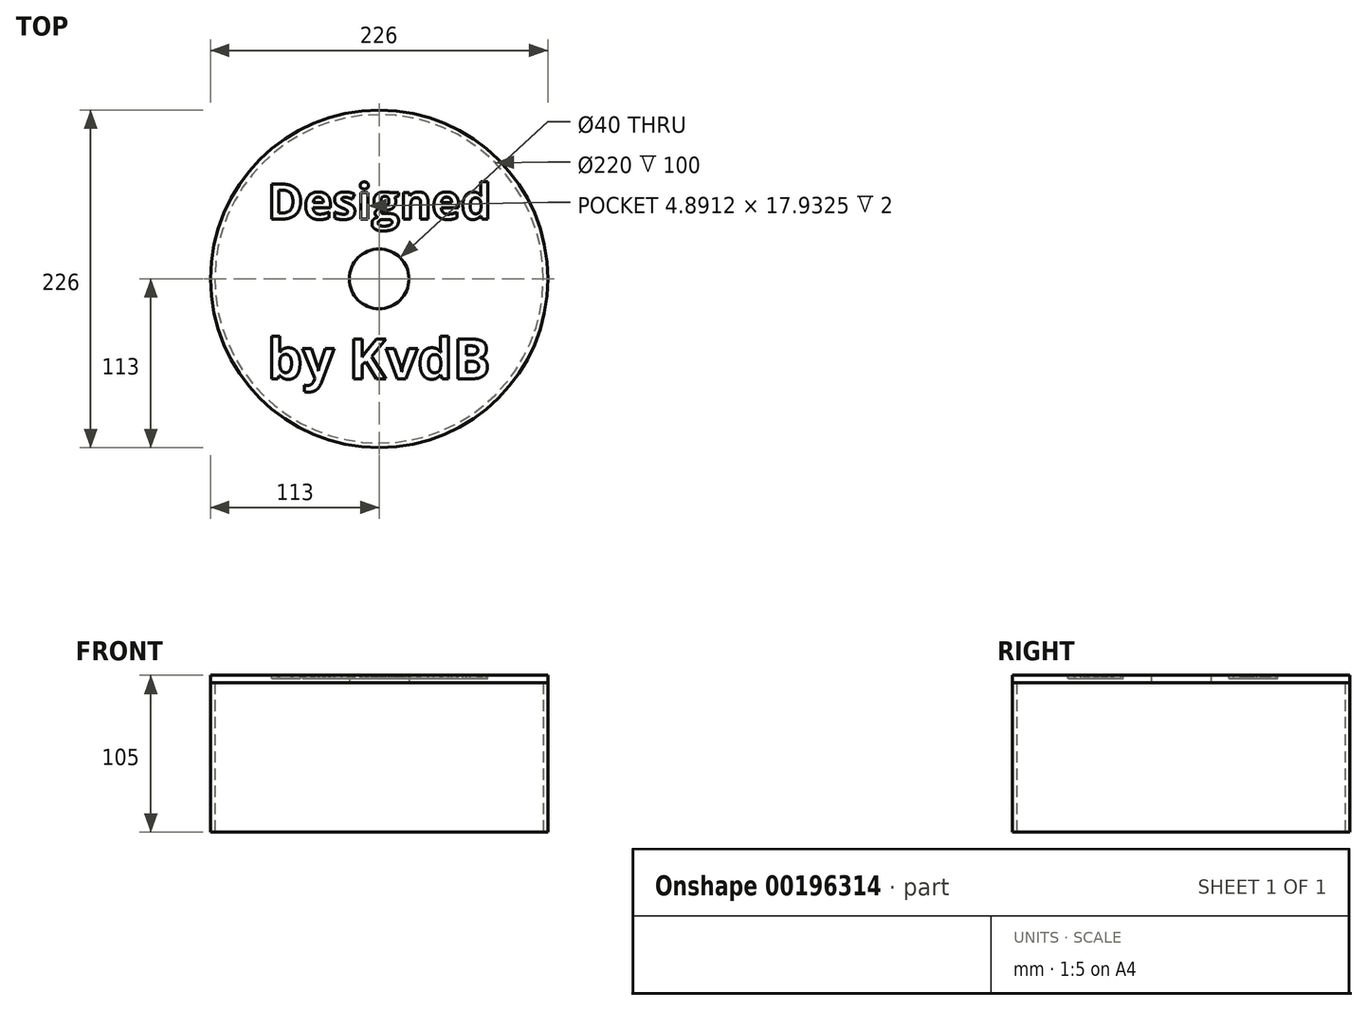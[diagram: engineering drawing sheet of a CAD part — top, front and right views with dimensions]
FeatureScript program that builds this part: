
annotation { "Feature Type Name" : "Feature", "Feature Type Description" : "" }
export const myFeature = defineFeature(function(context is Context, id is Id, definition is map)
    precondition{}
    {
        {
            var Q0;
            Q0=qCreatedBy(makeId("Top.planeOp"),FACE);
            var sketch = newSketch(context, id + "F0", { "sketchPlane" : qUnion([Q0])});
            skCircle(sketch, "E0", {"center": v(0, 0) * mm, "radius": 110 * mm});
            skCircle(sketch, "E1", {"center": v(0, 0) * mm, "radius": 113 * mm});
            skSolve(sketch);
        }
        {
            var Q0;
            Q0 = qSketchRegion(id + "F0", true);
            extrude(context, id + "F1", {"entities" : qUnion([Q0]), "depth" : 100 * mm});
        }
        {
            var Q0;
            Q0=makeQuery(id+"F1.opExtrude","CAP_FACE",FACE,{"disambiguationData":[OSD([sQuery(id+"F0.wireOp",EDGE,"E0"),sQuery(id+"F0.wireOp",EDGE,"E1")])],"isStart":false});
            var sketch = newSketch(context, id + "F2", { "sketchPlane" : qUnion([Q0])});
            skCircle(sketch, "E2", {"center": v(0, 0) * mm, "radius": 20 * mm});
            skSolve(sketch);
        }
        {
            var Q0;
            Q0=makeQuery(id+"F2.imprint","IMPRINT",FACE,{"disambiguationData":[TD([[makeQuery(id+"F2.imprint","IMPRINT",EDGE,{"derivedFrom":sQuery(id+"F2.wireOp",EDGE,"E2")}),-1.0]])]});
            var Q1;
            Q1=makeQuery(id+"F2.imprint","IMPRINT",FACE,{"disambiguationData":[TD([[makeQuery(id+"F2.imprint","IMPRINT",EDGE,{"derivedFrom":makeQuery(id+"F1.opExtrude","CAP_EDGE",EDGE,{"disambiguationData":[OSD([sQuery(id+"F0.wireOp",EDGE,"E0")])],"isStart":false})}),-1.0]])]});
            extrude(context, id + "F3", {"entities" : qUnion([Q0, Q1]), "depth" : 5 * mm});
        }
        {
            var Q0;
            Q0=makeQuery(id+"F3.opExtrude","CAP_FACE",FACE,{"disambiguationData":[OSD([sQuery(id+"F0.wireOp",EDGE,"E1"),sQuery(id+"F2.wireOp",EDGE,"E2")])],"isStart":false});
            var sketch = newSketch(context, id + "F4", { "sketchPlane" : qUnion([Q0])});
            skText(sketch, "E3", { "text": "Designed ", "fontName": "OpenSans-Bold.ttf"});
            skText(sketch, "E4", { "text": "by KvdB", "fontName": "OpenSans-Bold.ttf"});
            const initialGuessF4  = {"E3": [-0.075, 0.04, 1, 0, 0.02365], "E4": [-0.075, -0.06692, 1, 0, 0.02692]};
            skSetInitialGuess(sketch, initialGuessF4);
            skSolve(sketch);
        }
        {
            var Q0;
            Q0 = qSketchRegion(id + "F4", true);
            extrude(context, id + "F5", {"entities" : qUnion([Q0]), "operationType" : NewBodyOperationType.REMOVE, "oppositeDirection" : true, "depth" : 2 * mm});
        }
    });
